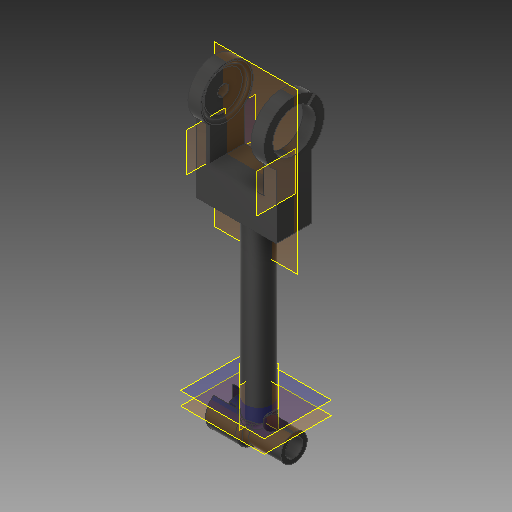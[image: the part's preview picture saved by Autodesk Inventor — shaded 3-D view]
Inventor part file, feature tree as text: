
AUTODESK INVENTOR PART (.ipt)
format: ipt  version: 2018 (Build 220112000, 112)  size: 664,064 bytes
history: native  units: mm
features: extrude x24, sketch x24, plane x8, other x6, fillet x5
ambient origin geometry x8: Origin, YZ Plane, XZ Plane, XY Plane, X Axis, Y Axis, Z Axis, Center Point
bodies: Body1 (feature_tree)
feature tree (67):
  other  "Sólido1"
  extrude  "Extrusión1"  Depth=40.0mm
  plane  "Plano de trabajo1"
  plane  "Plano de trabajo2"
  extrude  "Extrusión8"  Depth=24.5mm
  plane  "Plano de trabajo5"
  plane  "Plano de trabajo6"
  extrude  "Extrusión12"  Depth=10.0mm TaperAngle=0.0deg
  extrude  "Extrusión13"  Depth=6.3mm
  extrude  "Extrusión14"  Depth=24.5mm
  extrude  "Extrusión15"  Depth=1.6mm
  extrude  "Extrusión16"  Depth=4.0mm
  extrude  "Extrusión23"  Depth=20.0mm
  extrude  "Extrusión27"  Depth=10.0mm
  extrude  "Extrusión28"  Depth=25.0mm TaperAngle=0.0deg
  extrude  "Extrusión29"  Depth=10.0mm TaperAngle=0.0deg
  extrude  "Extrusión30"  Depth=100.0mm TaperAngle=0.0deg
  plane  "Plano de trabajo7"
  plane  "Plano de trabajo8"
  plane  "Plano de trabajo9"
  extrude  "Extrusión31"  Depth=20.0mm TaperAngle=0.0deg
  extrude  "Extrusión32"  Depth=20.0mm TaperAngle=0.0deg
  sketch  "Boceto40"  dims[d147=2.0mm d150=3.9mm]
  extrude  "Extrusión35"  Depth=3.9mm
  extrude  "Extrusion37"  Depth=2.0mm
  plane  "Work Plane10"
  sketch  "Sketch44"  dims[d153=3.9mm d154=7.9mm d155=0.0mm]
  extrude  "Extrusión40"  Depth=7.9mm TaperAngle=0.0deg
  sketch  "Boceto46"  dims[d171=5.5mm d172=5.0mm d173=10.0mm]
  extrude  "Extrusión43"  Depth=10.0mm TaperAngle=0.0deg
  extrude  "Extrusión44"  Depth=10.0mm
  other  "Edición directa1"
  fillet  "Empalme13"  Radius=10.0mm
  extrude  "Extrusión45"  Depth=20.0mm TaperAngle=0.0deg
  fillet  "Empalme14"  Radius=11.0mm
  fillet  "Empalme15"  Radius=2.0mm
  fillet  "Empalme16"  Radius=2.0mm
  fillet  "Empalme17"  Radius=24.0mm
  extrude  "Extrusión46"  Depth=7.0mm TaperAngle=0.0deg
  extrude  "Extrusión47"  Depth=3.0mm
  extrude  "Extrusión48"  Depth=2.0mm
  extrude  "Extrusión49"  Depth=2.0mm
  sketch  "Boceto1"  dims[d0=40.0mm d1=20.0mm]
  sketch  "Boceto8"  dims[d2=5.0mm d3=0.0mm d28=24.5mm]
  sketch  "Boceto17"  dims[d30=10.0mm d31=0.0mm d53=5.0mm d54=0.0mm]
  sketch  "Boceto18"  dims[d55=3.0mm d56=0.0mm d58=6.3mm]
  sketch  "Boceto19"  dims[d59=8.0mm d60=0.0mm d61=24.5mm]
  sketch  "Boceto20"  dims[d62=5.0mm d63=0.0mm d64=1.6mm]
  sketch  "Boceto21"  dims[d65=2.0mm d66=0.0mm d99=4.0mm]
  sketch  "Boceto28"  dims[d100=25.0mm d101=0.0mm d117=20.0mm]
  sketch  "Boceto32"  dims[d118=90.0deg d119=10.0mm]
  sketch  "Boceto33"  dims[d120=5.0mm d121=25.0mm d122=0.0mm]
  sketch  "Boceto34"  dims[d123=10.0mm d124=0.0mm d125=20.0mm d126=0.0mm]
  sketch  "Boceto35"  dims[d127=15.0mm d128=100.0mm d129=0.0mm]
  sketch  "Boceto38"  dims[d133=20.0mm d134=20.0mm d135=0.0mm]
  sketch  "Boceto39"  dims[d136=14.8mm d137=20.0mm d138=0.0mm]
  sketch  "Boceto42"  dims[d151=2.0mm d152=2.0mm]
  sketch  "Boceto45"  dims[d162=10.0mm d163=10.0mm d164=0.0mm]
  sketch  "Boceto48"  dims[d178=15.0mm d179=20.0mm d180=0.0mm d190=11.0mm d191=0.0mm d192=2.0mm d193=0.0mm]
  sketch  "Boceto49"  dims[d197=0.0mm d198=0.0mm d199=-3.0mm]
  sketch  "Boceto50"  dims[d200=0.0mm d201=0.0mm d202=-3.0mm]
  sketch  "Boceto51"  dims[d203=0.0mm d204=0.0mm d205=2.0mm]
  sketch  "Boceto52"  dims[d206=0.0mm d207=0.0mm d208=30.0mm d209=2.0mm d210=24.0mm d211=7.0mm d212=0.0mm d213=3.0mm d214=2.0mm d215=2.0mm d216=2.0mm d217=0.5mm d218=0.5mm d219=7.9mm d220=0.0mm d221=7.9mm d222=0.0mm d223=5.9mm d224=0.8mm d225=0.8mm d226=5.0mm d227=0.0mm d230=7.0mm d231=0.0mm]
  other  "Desplazar1"
  other  "Desplazar2"
  other  "Desplazar3"
  other  "Desplazar4"
